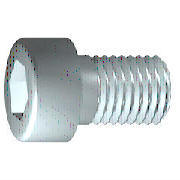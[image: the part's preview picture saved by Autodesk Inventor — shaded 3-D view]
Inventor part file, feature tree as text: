
AUTODESK INVENTOR PART (.ipt)
format: ipt  version: 2015 (Build 190159000, 159)  size: 195,584 bytes
history: native  units: mm (DEFAULTED — no unit token found)
features: sketch x2, extrude x1, plane x1, fillet x1
ambient origin geometry x7: Origin, YZ Plane, XY Plane, X Axis, Y Axis, Z Axis, Center Point
bodies: Solid1 (feature_tree), Body (feature_tree)
feature tree (5):
  extrude  "Slot"  Depth=5.0mm
  plane  "Work Plane1"
  fillet  "Fillet2"  Radius=5.0mm
  sketch  "Sketch1"  dims[d1=18.0mm d2=0.49086mm d3=5.0mm]
  sketch  "Sketch2"  dims[d4=2.5mm d5=60.0deg d6=5.0mm d7=5.0mm d8=4.618802mm d9=8.5mm d10=90.0deg d11=10.0mm d12=0.0mm d13=18.0mm d14=0.0mm d15=0.49076mm d16=0.49076mm d17=0.5mm d19=0.0mm d26=20.0mm d27=45.0deg d28=0.0mm d29=0.0mm d30=0.1mm]
